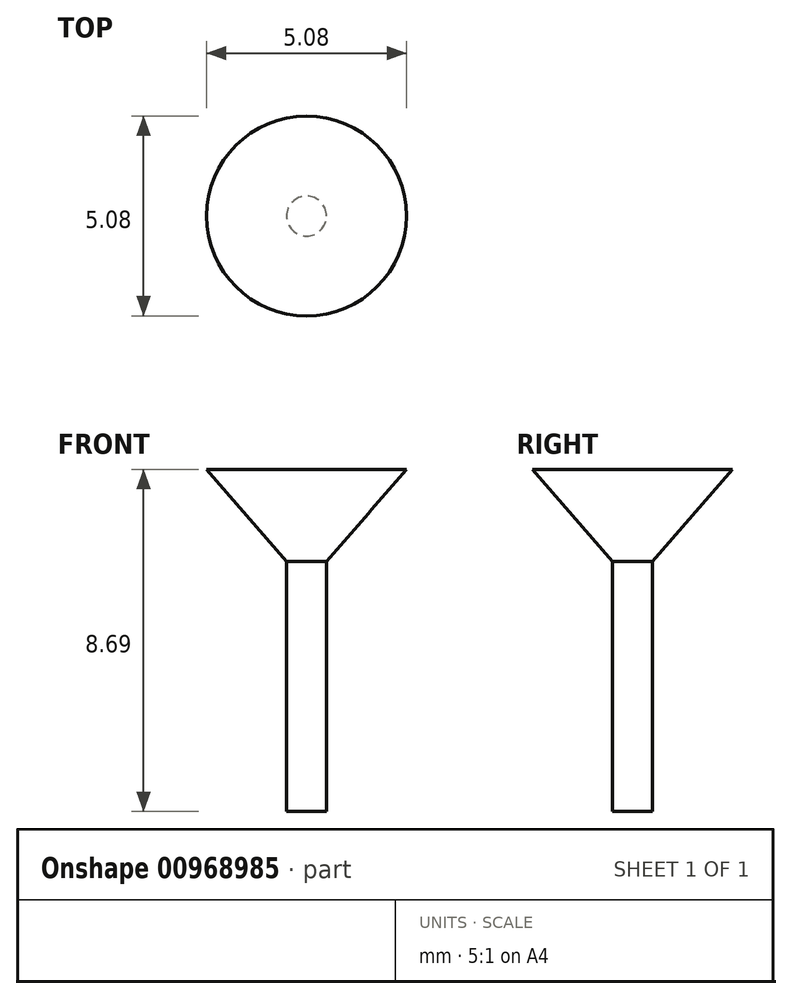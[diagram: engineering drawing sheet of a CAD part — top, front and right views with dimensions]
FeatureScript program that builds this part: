
annotation { "Feature Type Name" : "Feature", "Feature Type Description" : "" }
export const myFeature = defineFeature(function(context is Context, id is Id, definition is map)
    precondition{}
    {
        {
            var Q0;
            Q0=qCreatedBy(makeId("Front.planeOp"),FACE);
            var sketch = newSketch(context, id + "F0", { "sketchPlane" : qUnion([Q0])});
            skLineSegment(sketch, "E0", {"start": v(0, 0) * mm, "end": v(-0.5, 0) * mm});
            skLineSegment(sketch, "E1", {"start": v(-0.5, 0) * mm, "end": v(-0.5, 6.35) * mm});
            skLineSegment(sketch, "E2", {"start": v(-0.5, 6.35) * mm, "end": v(-2.54, 8.69) * mm});
            skLineSegment(sketch, "E3", {"start": v(-2.54, 8.69) * mm, "end": v(0, 8.69) * mm});
            skLineSegment(sketch, "E4", {"start": v(0, 8.69) * mm, "end": v(0, 0) * mm});
            skSolve(sketch);
        }
        {
            var Q0;
            Q0=makeQuery(id+"F0.imprint","IMPRINT",FACE,{"disambiguationData":[TD([[makeQuery(id+"F0.imprint","IMPRINT",EDGE,{"derivedFrom":sQuery(id+"F0.wireOp",EDGE,"E0")}),-1.0]])]});
            var Q1;
            Q1=sQuery(id+"F0.wireOp",EDGE,"E4");
            revolve(context, id + "F1", {"surfaceOperationType" : NewSurfaceOperationType.NEW, "entities" : qUnion([Q0]), "axis" : qUnion([Q1]), "revolveType" : RevolveType.FULL});
        }
    });
